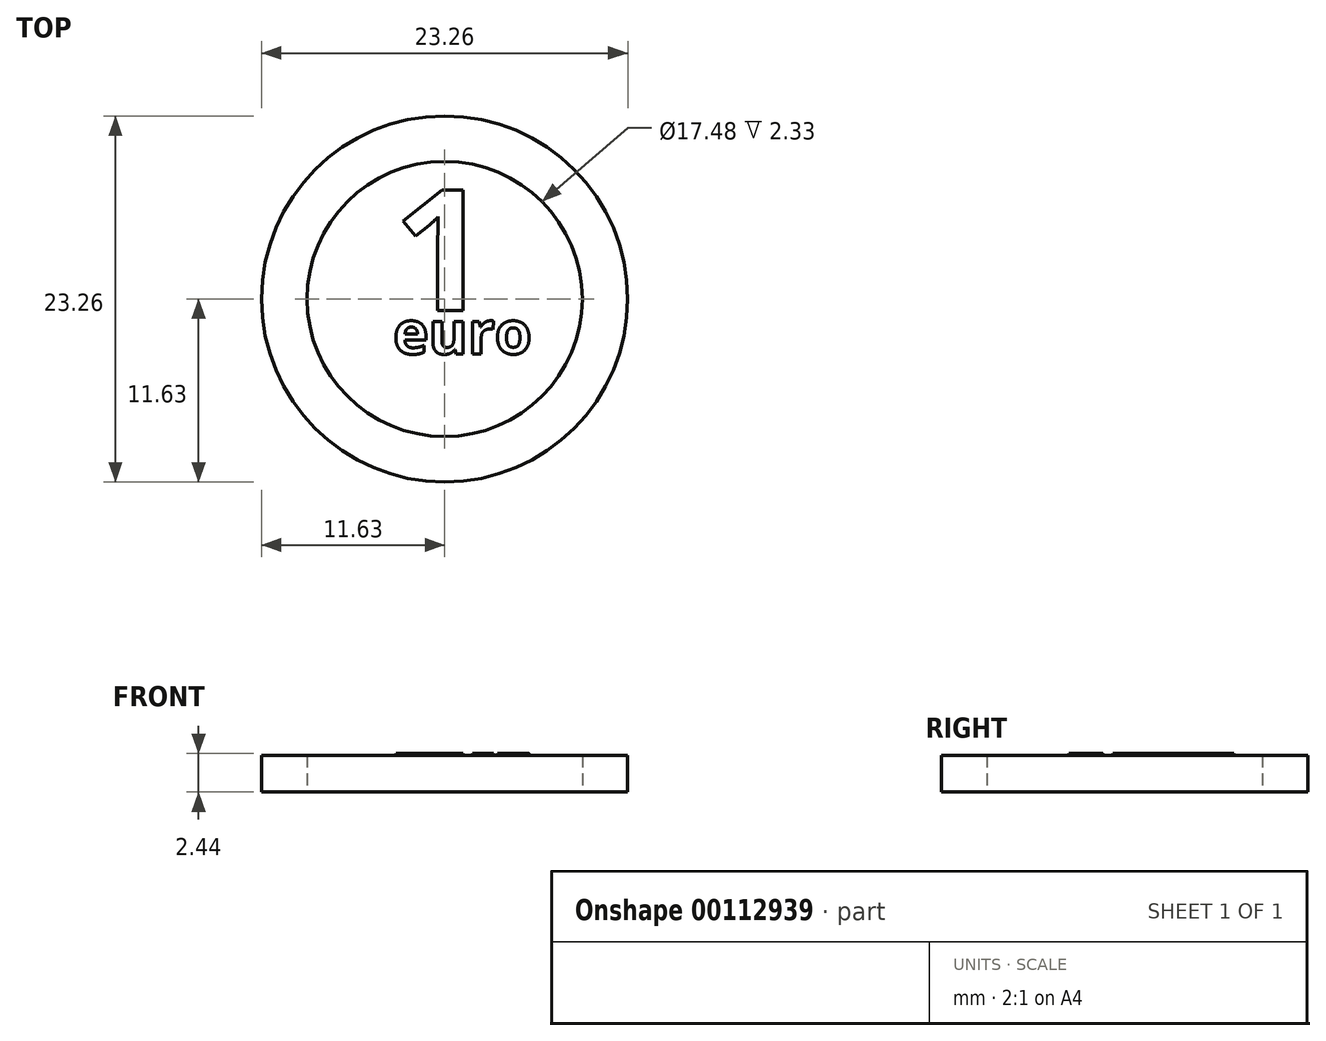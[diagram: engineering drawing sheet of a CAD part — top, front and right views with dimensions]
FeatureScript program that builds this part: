
annotation { "Feature Type Name" : "Feature", "Feature Type Description" : "" }
export const myFeature = defineFeature(function(context is Context, id is Id, definition is map)
    precondition{}
    {
        {
            var Q0;
            Q0=qCreatedBy(makeId("Top.planeOp"),FACE);
            var sketch = newSketch(context, id + "F0", { "sketchPlane" : qUnion([Q0])});
            skCircle(sketch, "E0", {"center": v(0, 0) * mm, "radius": 11.62 * mm});
            skCircle(sketch, "E1", {"center": v(0, 0) * mm, "radius": 8.74 * mm});
            skText(sketch, "E2", { "text": "1", "fontName": "OpenSans-Bold.ttf"});
            skText(sketch, "E3", { "text": "euro", "fontName": "OpenSans-Bold.ttf"});
            const initialGuessF0  = {"E2": [-0.00327, -0.00075, 1, 0, 0.00774], "E3": [-0.00327, -0.00349, 1, 0, 0.00273]};
            skSetInitialGuess(sketch, initialGuessF0);
            skSolve(sketch);
        }
        {
            var Q0;
            Q0=makeQuery(id+"F0.imprint","IMPRINT",FACE,{"disambiguationData":[TD([[makeQuery(id+"F0.imprint","IMPRINT",EDGE,{"derivedFrom":sQuery(id+"F0.wireOp",EDGE,"E0")}),1.0]])]});
            extrude(context, id + "F1", {"entities" : qUnion([Q0]), "depth" : 2.33 * mm});
        }
        {
            var Q0;
            Q0=makeQuery(id+"F0.imprint","IMPRINT",FACE,{"disambiguationData":[TD([[makeQuery(id+"F0.imprint","IMPRINT",EDGE,{"derivedFrom":sQuery(id+"F0.wireOp",EDGE,"E2.sketch_text.stroke-0")}),-1.0]])]});
            var Q1;
            Q1=makeQuery(id+"F0.imprint","IMPRINT",FACE,{"disambiguationData":[TD([[makeQuery(id+"F0.imprint","IMPRINT",EDGE,{"derivedFrom":sQuery(id+"F0.wireOp",EDGE,"E3.sketch_text.stroke-0")}),1.0]])]});
            var Q2;
            Q2=makeQuery(id+"F0.imprint","IMPRINT",FACE,{"disambiguationData":[TD([[makeQuery(id+"F0.imprint","IMPRINT",EDGE,{"derivedFrom":sQuery(id+"F0.wireOp",EDGE,"E3.sketch_text.stroke-50")}),1.0]])]});
            var Q3;
            Q3=makeQuery(id+"F0.imprint","IMPRINT",FACE,{"disambiguationData":[TD([[makeQuery(id+"F0.imprint","IMPRINT",EDGE,{"derivedFrom":sQuery(id+"F0.wireOp",EDGE,"E3.sketch_text.stroke-0")}),-1.0]])]});
            var Q4;
            Q4=makeQuery(id+"F0.imprint","IMPRINT",FACE,{"disambiguationData":[TD([[makeQuery(id+"F0.imprint","IMPRINT",EDGE,{"derivedFrom":sQuery(id+"F0.wireOp",EDGE,"E3.sketch_text.stroke-20")}),-1.0]])]});
            var Q5;
            Q5=makeQuery(id+"F0.imprint","IMPRINT",FACE,{"disambiguationData":[TD([[makeQuery(id+"F0.imprint","IMPRINT",EDGE,{"derivedFrom":sQuery(id+"F0.wireOp",EDGE,"E3.sketch_text.stroke-37")}),-1.0]])]});
            var Q6;
            Q6=makeQuery(id+"F0.imprint","IMPRINT",FACE,{"disambiguationData":[TD([[makeQuery(id+"F0.imprint","IMPRINT",EDGE,{"derivedFrom":sQuery(id+"F0.wireOp",EDGE,"E3.sketch_text.stroke-50")}),-1.0]])]});
            var Q7;
            Q7=makeQuery(id+"F0.imprint","IMPRINT",FACE,{"disambiguationData":[TD([[makeQuery(id+"F0.imprint","IMPRINT",EDGE,{"derivedFrom":sQuery(id+"F0.wireOp",EDGE,"E1")}),1.0]])]});
            extrude(context, id + "F2", {"entities" : qUnion([Q0, Q1, Q2, Q3, Q4, Q5, Q6, Q7]), "depth" : 2.33 * mm});
        }
        {
            var Q0;
            Q0=makeQuery(id+"F0.imprint","IMPRINT",FACE,{"disambiguationData":[TD([[makeQuery(id+"F0.imprint","IMPRINT",EDGE,{"derivedFrom":sQuery(id+"F0.wireOp",EDGE,"E3.sketch_text.stroke-0")}),-1.0]])]});
            var Q1;
            Q1=makeQuery(id+"F0.imprint","IMPRINT",FACE,{"disambiguationData":[TD([[makeQuery(id+"F0.imprint","IMPRINT",EDGE,{"derivedFrom":sQuery(id+"F0.wireOp",EDGE,"E3.sketch_text.stroke-20")}),-1.0]])]});
            var Q2;
            Q2=makeQuery(id+"F0.imprint","IMPRINT",FACE,{"disambiguationData":[TD([[makeQuery(id+"F0.imprint","IMPRINT",EDGE,{"derivedFrom":sQuery(id+"F0.wireOp",EDGE,"E3.sketch_text.stroke-37")}),-1.0]])]});
            var Q3;
            Q3=makeQuery(id+"F0.imprint","IMPRINT",FACE,{"disambiguationData":[TD([[makeQuery(id+"F0.imprint","IMPRINT",EDGE,{"derivedFrom":sQuery(id+"F0.wireOp",EDGE,"E2.sketch_text.stroke-0")}),-1.0]])]});
            var Q4;
            Q4=makeQuery(id+"F0.imprint","IMPRINT",FACE,{"disambiguationData":[TD([[makeQuery(id+"F0.imprint","IMPRINT",EDGE,{"derivedFrom":sQuery(id+"F0.wireOp",EDGE,"E3.sketch_text.stroke-50")}),-1.0]])]});
            extrude(context, id + "F3", {"entities" : qUnion([Q0, Q1, Q2, Q3, Q4]), "operationType" : NewBodyOperationType.ADD, "depth" : 2.44 * mm});
        }
    });
